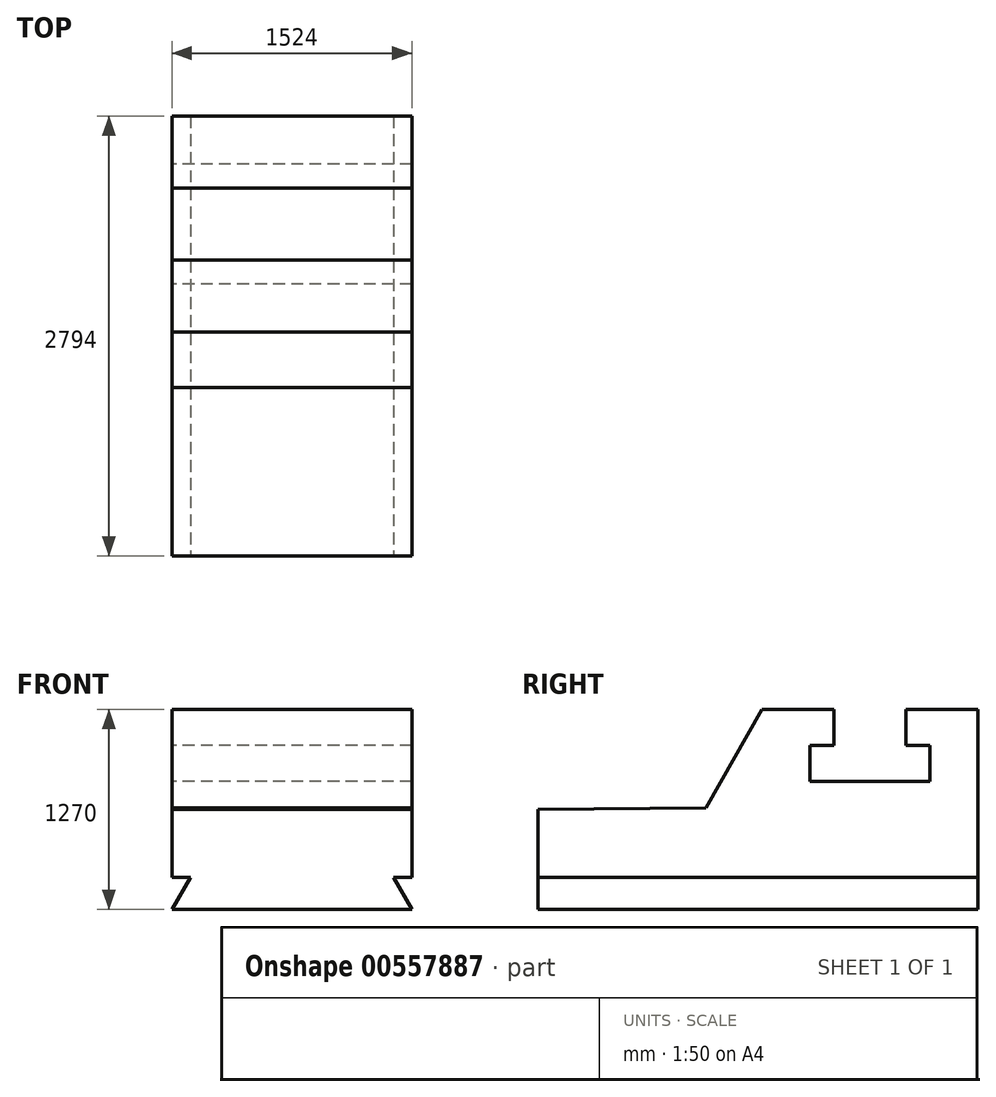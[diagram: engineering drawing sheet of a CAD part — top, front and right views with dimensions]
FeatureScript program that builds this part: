
annotation { "Feature Type Name" : "Feature", "Feature Type Description" : "" }
export const myFeature = defineFeature(function(context is Context, id is Id, definition is map)
    precondition{}
    {
        {
            var Q0;
            Q0=qCreatedBy(makeId("Right.planeOp"),FACE);
            var sketch = newSketch(context, id + "F0", { "sketchPlane" : qUnion([Q0])});
            skLineSegment(sketch, "E0", {"start": v(-101.11, -56.99) * mm, "end": v(2692.89, -56.99) * mm});
            skLineSegment(sketch, "E1", {"start": v(2692.89, -56.99) * mm, "end": v(2692.89, 1213.01) * mm});
            skLineSegment(sketch, "E2", {"start": v(2692.89, 1213.01) * mm, "end": v(2235.69, 1213.01) * mm});
            skLineSegment(sketch, "E3", {"start": v(2235.69, 1213.01) * mm, "end": v(2235.69, 984.41) * mm});
            skLineSegment(sketch, "E4", {"start": v(2235.69, 984.41) * mm, "end": v(2388.09, 984.41) * mm});
            skLineSegment(sketch, "E5", {"start": v(2388.09, 984.41) * mm, "end": v(2388.09, 755.81) * mm});
            skLineSegment(sketch, "E6", {"start": v(2388.09, 755.81) * mm, "end": v(1626.09, 755.81) * mm});
            skLineSegment(sketch, "E7", {"start": v(1626.09, 755.81) * mm, "end": v(1626.09, 984.41) * mm});
            skLineSegment(sketch, "E8", {"start": v(1626.09, 984.41) * mm, "end": v(1778.49, 984.41) * mm});
            skLineSegment(sketch, "E9", {"start": v(1778.49, 984.41) * mm, "end": v(1778.49, 1213.01) * mm});
            skLineSegment(sketch, "E10", {"start": v(1778.49, 1213.01) * mm, "end": v(1321.29, 1213.01) * mm});
            skLineSegment(sketch, "E11", {"start": v(-101.11, -56.99) * mm, "end": v(-101.11, 578.01) * mm});
            skLineSegment(sketch, "E12", {"start": v(1321.29, 1213.01) * mm, "end": v(967.47, 587.47) * mm});
            skLineSegment(sketch, "E13", {"start": v(967.47, 587.47) * mm, "end": v(-101.11, 578.01) * mm});
            skSolve(sketch);
        }
        {
            var Q0;
            Q0=makeQuery(id+"F0.imprint","IMPRINT",FACE,{"disambiguationData":[TD([[makeQuery(id+"F0.imprint","IMPRINT",EDGE,{"derivedFrom":sQuery(id+"F0.wireOp",EDGE,"E0")}),1.0]])]});
            extrude(context, id + "F1", {"entities" : qUnion([Q0]), "depth" : 1524 * mm, "offsetDistance" : 25.4 * mm});
        }
        {
            var Q0;
            Q0=makeQuery(id+"F1.opExtrude","SWEPT_FACE",FACE,{"disambiguationData":[OSD([sQuery(id+"F0.wireOp",EDGE,"E11")])]});
            var sketch = newSketch(context, id + "F2", { "sketchPlane" : qUnion([Q0])});
            skLineSegment(sketch, "E14", {"start": v(1524, -56.99) * mm, "end": v(1524, 146.21) * mm});
            skLineSegment(sketch, "E15", {"start": v(1524, 146.21) * mm, "end": v(1406.68, 146.21) * mm});
            skLineSegment(sketch, "E16", {"start": v(1406.68, 146.21) * mm, "end": v(1524, -56.99) * mm});
            skLineSegment(sketch, "E17", {"start": v(0, -56.99) * mm, "end": v(0, 146.21) * mm});
            skLineSegment(sketch, "E18", {"start": v(0, 146.21) * mm, "end": v(117.32, 146.21) * mm});
            skLineSegment(sketch, "E19", {"start": v(117.32, 146.21) * mm, "end": v(0, -56.99) * mm});
            skSolve(sketch);
        }
        {
            var Q0;
            Q0=makeQuery(id+"F2.imprint","IMPRINT",FACE,{"disambiguationData":[TD([[makeQuery(id+"F2.imprint","IMPRINT",EDGE,{"derivedFrom":sQuery(id+"F2.wireOp",EDGE,"E14")}),1.0]])]});
            var Q1;
            Q1=makeQuery(id+"F2.imprint","IMPRINT",FACE,{"disambiguationData":[TD([[makeQuery(id+"F2.imprint","IMPRINT",EDGE,{"derivedFrom":sQuery(id+"F2.wireOp",EDGE,"E17")}),-1.0]])]});
            extrude(context, id + "F3", {"entities" : qUnion([Q0, Q1]), "operationType" : NewBodyOperationType.REMOVE, "endBound" : BoundingType.THROUGH_ALL, "oppositeDirection" : true, "depth" : 25.4 * mm, "offsetDistance" : 25.4 * mm});
        }
    });
